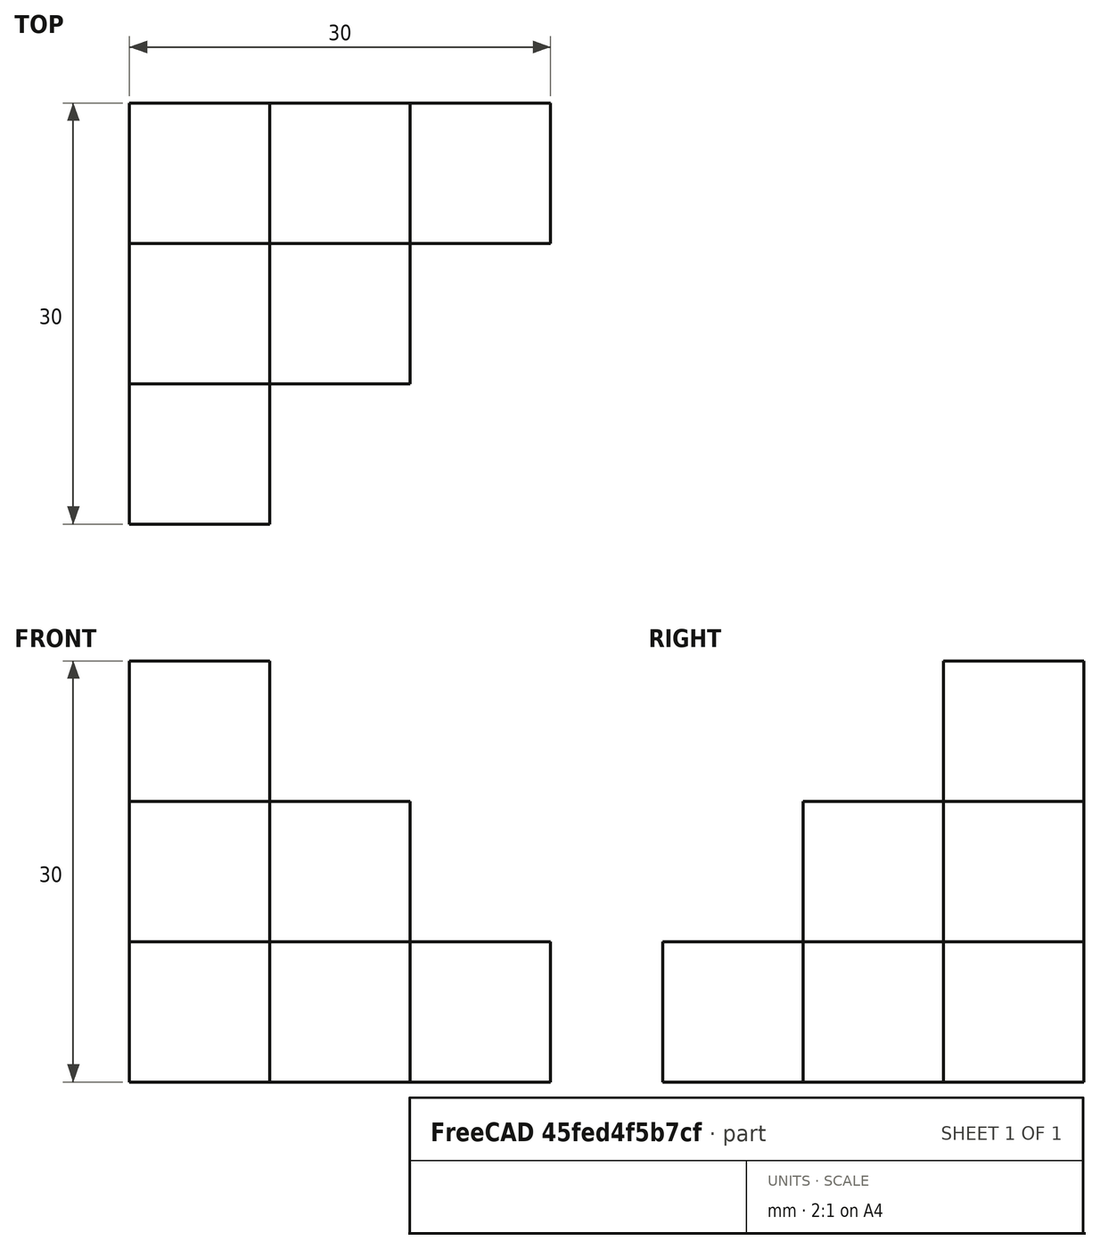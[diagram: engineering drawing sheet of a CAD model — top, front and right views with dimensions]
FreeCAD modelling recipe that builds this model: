
FCSTD DOCUMENT  (FreeCAD 0.21R33694 (Git))
Label: OJT1_T05R02_qubert3
License: All rights reserved
LicenseURL: http://en.wikipedia.org/wiki/All_rights_reserved
objects: Part::Box×6, Part::MultiFuse×1
note: 7 computed .brp shape members not serialized (recipe doc carries the construction recipe); baked Part::Feature solids carry a one-line shape summary decoded from their .brp

FEATURE [Part::Box] Box  label="cubo1"
  AttacherType = Attacher::AttachEngine3D
  Height = 30
  Length = 10
  Width = 10
FEATURE [Part::Box] Box001  label="cubo2"
  AttacherType = Attacher::AttachEngine3D
  Height = 20
  Length = 10
  Placement = pos=(10,0,0) rot=(0,0,1;0rad)
  Width = 10
FEATURE [Part::Box] Box002  label="cubo3"
  AttacherType = Attacher::AttachEngine3D
  Height = 20
  Length = 10
  Placement = pos=(0,-10,0) rot=(0,0,1;0rad)
  Width = 10
FEATURE [Part::Box] Box003  label="cubo4"
  AttacherType = Attacher::AttachEngine3D
  Height = 10
  Length = 10
  Placement = pos=(10,-10,0) rot=(0,0,1;0rad)
  Width = 10
FEATURE [Part::Box] Box004  label="cubo5"
  AttacherType = Attacher::AttachEngine3D
  Height = 10
  Length = 10
  Placement = pos=(20,0,0) rot=(0,0,1;0rad)
  Width = 10
FEATURE [Part::Box] Box005  label="cubo6"
  AttacherType = Attacher::AttachEngine3D
  Height = 10
  Length = 10
  Placement = pos=(0,-20,0) rot=(0,0,1;0rad)
  Width = 10
FEATURE [Part::MultiFuse] Fusion
  Refine = true
  Shapes = -> [Box,Box001,Box002,Box003,Box004,Box005]
